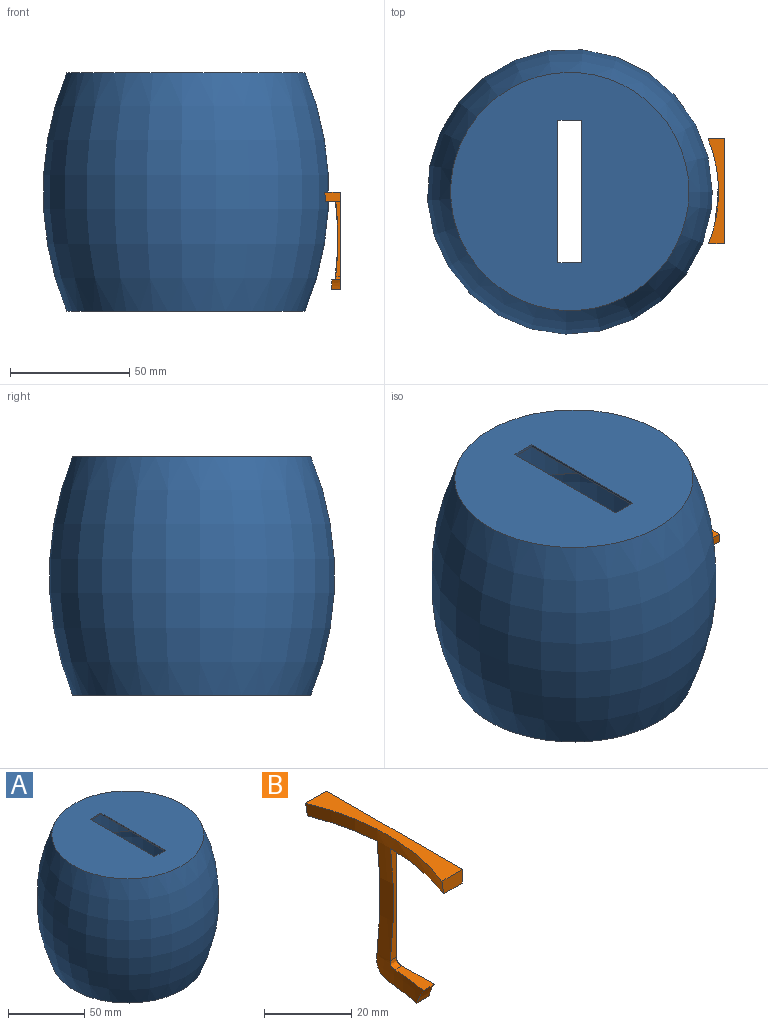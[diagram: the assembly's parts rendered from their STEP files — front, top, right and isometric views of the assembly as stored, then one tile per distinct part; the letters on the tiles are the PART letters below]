
ASSEMBLY  parts=2 mates=1
PART A: 13 faces, bbox 120x120x100 mm
  f0: plane 95x95mm, normal (0,0,-1), area 6488.2mm2, adj f6,f7,f8,f9,f10
  f1: plane 100x100mm, normal (0,0,1), area 7254mm2, adj f3,f6,f7,f8,f9
  f2: plane 100x100mm, normal (0,0,-1), area 336.9mm2, adj f3,f5
  f3: revolved ~120x120mm, area 36535.5mm2, adj f1,f2
  f4: plane 98.66x98.66mm, normal (0,0,-1), area 407.1mm2, adj f5,f11
  f5: revolved ~118x118mm, area 35553.4mm2, adj f2,f4
  f6: plane 10x1mm, normal (0,1,0), area 10mm2, adj f0,f1,f7,f9
  f7: plane 60x1mm, normal (-1,0,0), area 60mm2, adj f0,f1,f6,f8
  f8: plane 10x1mm, normal (0,-1,0), area 10mm2, adj f0,f1,f7,f9
  f9: plane 60x1mm, normal (1,0,0), area 60mm2, adj f0,f1,f6,f8
  f10: cylinder r=47.5mm len=95mm, axis (0,0,1), area 8953.5mm2, adj f0,f12
  f11: cylinder r=48mm len=96mm, axis (0,0,1), area 9047.8mm2, adj f4,f12
  f12: plane 96x96mm, normal (0,0,-1), area 150mm2, adj f10,f11
PART B: 14 faces, bbox 357.2x356.1x277.3 mm
  f0: plane 6.83x3.84mm, normal (0,1,0), area 25mm2, adj f9,f11,f12,f13
  f1: plane 6.66x3.85mm, normal (0,-1,0), area 24.3mm2, adj f9,f10,f12,f13
  f2: plane 267.66x238.16mm, normal (0,-1,0), area 41.5mm2, adj f3,f10,f12,f13
  f3: extruded ~2.22x1.66mm, area 5.6mm2, adj f2,f4,f12,f13
  f4: extruded ~10.59x3.55mm, area 28.9mm2, adj f3,f5,f12,f13
  f5: extruded ~4.23x3.84mm, area 17.1mm2, adj f4,f6,f12,f13
  f6: extruded ~11.7x3.84mm, area 36.5mm2, adj f5,f7,f12,f13
  f7: extruded ~4.89x2.97mm, area 14.9mm2, adj f6,f8,f12,f13
  f8: plane 267.82x238.4mm, normal (0,1,0), area 45.3mm2, adj f7,f11,f12,f13
  f9: plane 43.95x6.81mm, normal (0,0,1), area 169.5mm2, adj f0,f1,f12,f13
  f10: plane 21.32x6.09mm, normal (0,0,-1), area 70.9mm2, adj f1,f2,f12,f13
  f11: plane 254.67x242.53mm, normal (0,0,-1), area 66.9mm2, adj f0,f8,f12,f13
  f12: plane 43.95x40.98mm, normal (1,0,0), area 365.1mm2, adj f0,f1,f2,f3,f4,f5,f6,f7
  f13: revolved ~119.87x119.83mm, area 9174.9mm2, adj f0,f1,f2,f3,f4,f5,f6,f7
PLACE A t=(-0.36,0.1,68.66)mm
PLACE B t=(3.54,0.1,49.29)mm
MATE planar B.f9 <-> A.f10  axis (0,0,1) through (3.54,0.1,68.66)mm
